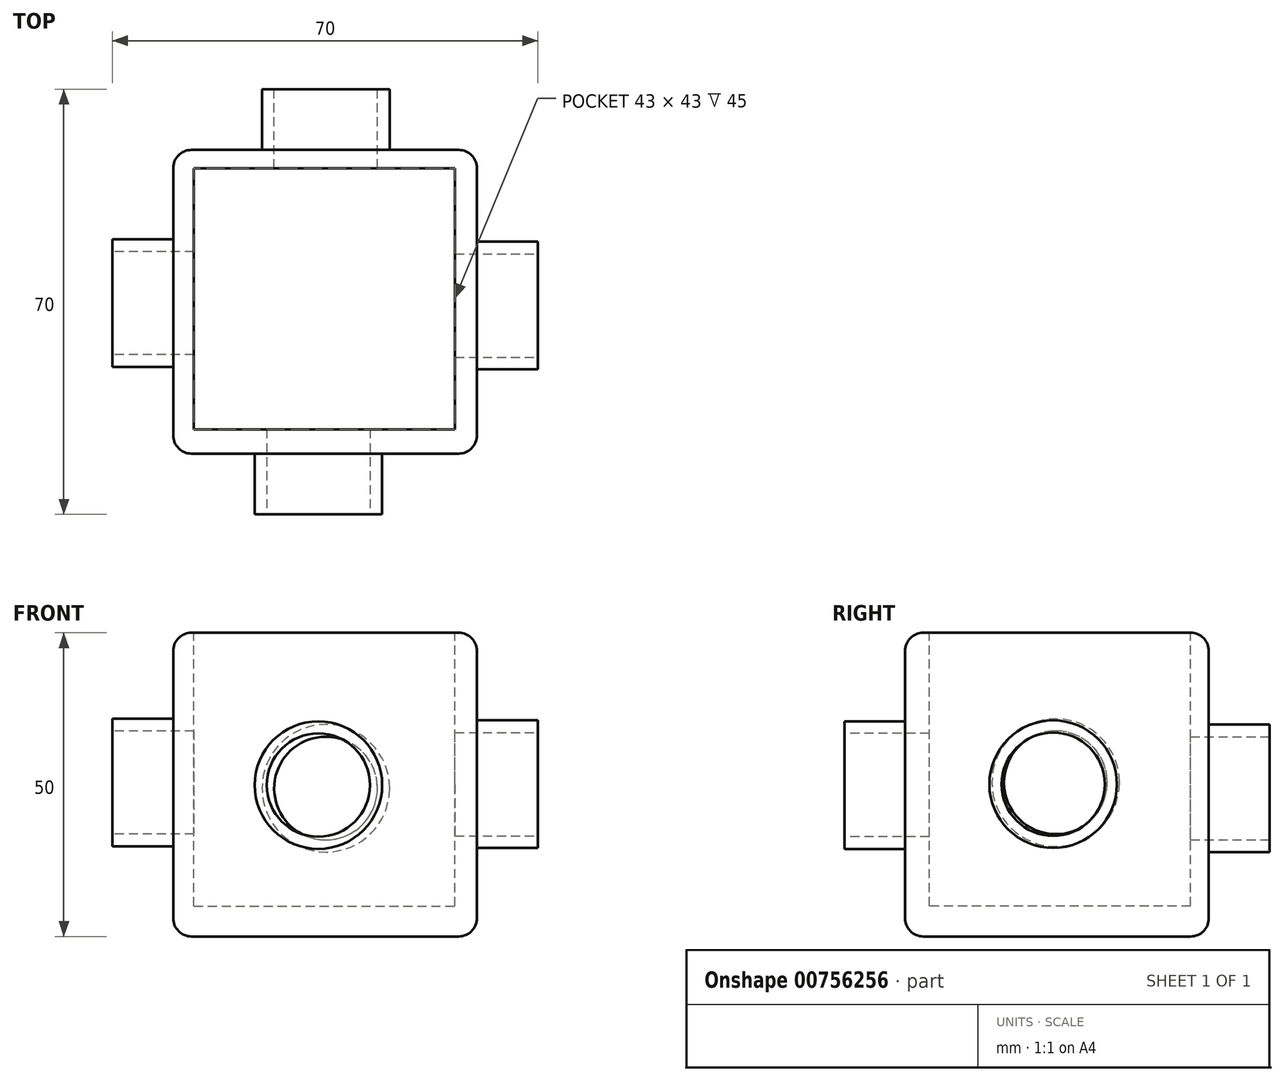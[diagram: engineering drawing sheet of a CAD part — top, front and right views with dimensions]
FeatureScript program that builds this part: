
annotation { "Feature Type Name" : "Feature", "Feature Type Description" : "" }
export const myFeature = defineFeature(function(context is Context, id is Id, definition is map)
    precondition{}
    {
        {
            var Q0;
            Q0=qCreatedBy(makeId("Top.planeOp"),FACE);
            var sketch = newSketch(context, id + "F0", { "sketchPlane" : qUnion([Q0])});
            skLineSegment(sketch, "E0.bottom", {"start": v(-55.44, -10.91) * mm, "end": v(-5.44, -10.91) * mm});
            skLineSegment(sketch, "E0.top", {"start": v(-55.44, -60.91) * mm, "end": v(-5.44, -60.91) * mm});
            skLineSegment(sketch, "E0.left", {"start": v(-55.44, -10.91) * mm, "end": v(-55.44, -60.91) * mm});
            skLineSegment(sketch, "E0.right", {"start": v(-5.44, -10.91) * mm, "end": v(-5.44, -60.91) * mm});
            skSolve(sketch);
        }
        {
            var Q0;
            Q0=qSketchRegion(id+"F0",true);
            extrude(context, id + "F1", {"entities" : qUnion([Q0]), "depth" : 50 * mm, "offsetDistance" : 25 * mm});
        }
        {
            var Q0;
            Q0=makeQuery(id+"F1.opExtrude","CAP_FACE",FACE,{"disambiguationData":[OSD([sQuery(id+"F0.wireOp",EDGE,"E0.bottom"),sQuery(id+"F0.wireOp",EDGE,"E0.top"),sQuery(id+"F0.wireOp",EDGE,"E0.left"),sQuery(id+"F0.wireOp",EDGE,"E0.right")])],"isStart":false});
            var sketch = newSketch(context, id + "F2", { "sketchPlane" : qUnion([Q0])});
            skLineSegment(sketch, "E1.bottom", {"start": v(-55.44, -60.91) * mm, "end": v(-5.44, -60.91) * mm});
            skLineSegment(sketch, "E1.top", {"start": v(-55.44, -10.91) * mm, "end": v(-5.44, -10.91) * mm});
            skLineSegment(sketch, "E1.left", {"start": v(-55.44, -60.91) * mm, "end": v(-55.44, -10.91) * mm});
            skLineSegment(sketch, "E1.right", {"start": v(-5.44, -60.91) * mm, "end": v(-5.44, -10.91) * mm});
            skSolve(sketch);
        }
        {
            var Q0;
            Q0=makeQuery(id+"F2.imprint","IMPRINT",FACE,{"disambiguationData":[TD([[makeQuery(id+"F2.imprint","IMPRINT",EDGE,{"derivedFrom":sQuery(id+"F2.wireOp",EDGE,"E1.bottom")}),1.0]])]});
            var sketch = newSketch(context, id + "F3", { "sketchPlane" : qUnion([Q0])});
            skLineSegment(sketch, "E2.bottom", {"start": v(-52.06, -13.92) * mm, "end": v(-9.06, -13.92) * mm});
            skLineSegment(sketch, "E2.top", {"start": v(-52.06, -56.92) * mm, "end": v(-9.06, -56.92) * mm});
            skLineSegment(sketch, "E2.left", {"start": v(-52.06, -13.92) * mm, "end": v(-52.06, -56.92) * mm});
            skLineSegment(sketch, "E2.right", {"start": v(-9.06, -13.92) * mm, "end": v(-9.06, -56.92) * mm});
            skSolve(sketch);
        }
        {
            var Q0;
            Q0=qSketchRegion(id+"F3",true);
            extrude(context, id + "F4", {"entities" : qUnion([Q0]), "operationType" : NewBodyOperationType.REMOVE, "oppositeDirection" : true, "depth" : 45 * mm, "offsetDistance" : 25 * mm});
        }
        {
            var Q0;
            Q0=makeQuery(id+"F1.opExtrude","SWEPT_FACE",FACE,{"disambiguationData":[OSD([sQuery(id+"F0.wireOp",EDGE,"E0.top")])]});
            var sketch = newSketch(context, id + "F5", { "sketchPlane" : qUnion([Q0])});
            skCircle(sketch, "E3", {"center": v(-31.55, 24.92) * mm, "radius": 8.5 * mm});
            skSolve(sketch);
        }
        {
            var Q0;
            Q0=makeQuery(id+"F5.imprint","IMPRINT",FACE,{"disambiguationData":[TD([[makeQuery(id+"F5.imprint","IMPRINT",EDGE,{"derivedFrom":sQuery(id+"F5.wireOp",EDGE,"E3")}),1.0]])]});
            extrude(context, id + "F6", {"entities" : qUnion([Q0]), "operationType" : NewBodyOperationType.REMOVE, "oppositeDirection" : true, "depth" : 10 * mm, "offsetDistance" : 25 * mm});
        }
        {
            var Q0;
            Q0=makeQuery(id+"F1.opExtrude","SWEPT_FACE",FACE,{"disambiguationData":[OSD([sQuery(id+"F0.wireOp",EDGE,"E0.right")])]});
            var sketch = newSketch(context, id + "F7", { "sketchPlane" : qUnion([Q0])});
            skCircle(sketch, "E4", {"center": v(-36.54, 25.07) * mm, "radius": 8.5 * mm});
            skSolve(sketch);
        }
        {
            var Q0;
            Q0=qSketchRegion(id+"F7",true);
            extrude(context, id + "F8", {"entities" : qUnion([Q0]), "operationType" : NewBodyOperationType.REMOVE, "oppositeDirection" : true, "depth" : 7 * mm, "offsetDistance" : 25 * mm});
        }
        {
            var Q0;
            Q0=makeQuery(id+"F1.opExtrude","SWEPT_FACE",FACE,{"disambiguationData":[OSD([sQuery(id+"F0.wireOp",EDGE,"E0.bottom")])]});
            var sketch = newSketch(context, id + "F9", { "sketchPlane" : qUnion([Q0])});
            skCircle(sketch, "E5", {"center": v(30.32, 24.4) * mm, "radius": 8.5 * mm});
            skSolve(sketch);
        }
        {
            var Q0;
            Q0=qSketchRegion(id+"F9",true);
            extrude(context, id + "F10", {"entities" : qUnion([Q0]), "operationType" : NewBodyOperationType.REMOVE, "oppositeDirection" : true, "depth" : 7 * mm, "offsetDistance" : 25 * mm});
        }
        {
            var Q0;
            Q0=makeQuery(id+"F1.opExtrude","SWEPT_FACE",FACE,{"disambiguationData":[OSD([sQuery(id+"F0.wireOp",EDGE,"E0.left")])]});
            var sketch = newSketch(context, id + "F11", { "sketchPlane" : qUnion([Q0])});
            skCircle(sketch, "E6", {"center": v(36.13, 25.34) * mm, "radius": 8.5 * mm});
            skSolve(sketch);
        }
        {
            var Q0;
            Q0=qSketchRegion(id+"F11",true);
            extrude(context, id + "F12", {"entities" : qUnion([Q0]), "operationType" : NewBodyOperationType.REMOVE, "oppositeDirection" : true, "depth" : 7 * mm, "offsetDistance" : 25 * mm});
        }
        {
            var Q0;
            Q0=makeQuery(id+"F1.opExtrude","SWEPT_FACE",FACE,{"disambiguationData":[OSD([sQuery(id+"F0.wireOp",EDGE,"E0.left")])]});
            var sketch = newSketch(context, id + "F13", { "sketchPlane" : qUnion([Q0])});
            skCircle(sketch, "E7", {"center": v(36.13, 25.34) * mm, "radius": 10.5 * mm});
            skSolve(sketch);
        }
        {
            var Q0;
            Q0=makeQuery(id+"F13.imprint","IMPRINT",FACE,{"disambiguationData":[TD([[makeQuery(id+"F13.imprint","IMPRINT",EDGE,{"derivedFrom":sQuery(id+"F13.wireOp",EDGE,"E7")}),1.0]])]});
            extrude(context, id + "F14", {"entities" : qUnion([Q0]), "operationType" : NewBodyOperationType.ADD, "depth" : 10 * mm, "offsetDistance" : 25 * mm});
        }
        {
            var Q0;
            Q0=makeQuery(id+"F1.opExtrude","SWEPT_FACE",FACE,{"disambiguationData":[OSD([sQuery(id+"F0.wireOp",EDGE,"E0.top")])]});
            var sketch = newSketch(context, id + "F15", { "sketchPlane" : qUnion([Q0])});
            skCircle(sketch, "E8", {"center": v(-31.55, 24.92) * mm, "radius": 10.5 * mm});
            skSolve(sketch);
        }
        {
            var Q0;
            Q0=makeQuery(id+"F15.imprint","IMPRINT",FACE,{"disambiguationData":[TD([[makeQuery(id+"F15.imprint","IMPRINT",EDGE,{"derivedFrom":sQuery(id+"F15.wireOp",EDGE,"E8")}),1.0]])]});
            extrude(context, id + "F16", {"entities" : qUnion([Q0]), "operationType" : NewBodyOperationType.ADD, "depth" : 10 * mm, "offsetDistance" : 25 * mm});
        }
        {
            var Q0;
            Q0=makeQuery(id+"F1.opExtrude","SWEPT_FACE",FACE,{"disambiguationData":[OSD([sQuery(id+"F0.wireOp",EDGE,"E0.right")])]});
            var sketch = newSketch(context, id + "F17", { "sketchPlane" : qUnion([Q0])});
            skCircle(sketch, "E9", {"center": v(-36.54, 25.07) * mm, "radius": 10.5 * mm});
            skSolve(sketch);
        }
        {
            var Q0;
            Q0=makeQuery(id+"F17.imprint","IMPRINT",FACE,{"disambiguationData":[TD([[makeQuery(id+"F17.imprint","IMPRINT",EDGE,{"derivedFrom":sQuery(id+"F17.wireOp",EDGE,"E9")}),1.0]])]});
            extrude(context, id + "F18", {"entities" : qUnion([Q0]), "operationType" : NewBodyOperationType.ADD, "depth" : 10 * mm, "offsetDistance" : 25 * mm});
        }
        {
            var Q0;
            Q0=makeQuery(id+"F1.opExtrude","SWEPT_FACE",FACE,{"disambiguationData":[OSD([sQuery(id+"F0.wireOp",EDGE,"E0.bottom")])]});
            var sketch = newSketch(context, id + "F19", { "sketchPlane" : qUnion([Q0])});
            skCircle(sketch, "E10", {"center": v(30.32, 24.4) * mm, "radius": 10.5 * mm});
            skSolve(sketch);
        }
        {
            var Q0;
            Q0=makeQuery(id+"F19.imprint","IMPRINT",FACE,{"disambiguationData":[TD([[makeQuery(id+"F19.imprint","IMPRINT",EDGE,{"derivedFrom":sQuery(id+"F19.wireOp",EDGE,"E10")}),1.0]])]});
            extrude(context, id + "F20", {"entities" : qUnion([Q0]), "operationType" : NewBodyOperationType.ADD, "depth" : 10 * mm, "offsetDistance" : 25 * mm});
        }
        {
            var Q0;
            Q0=makeQuery(id+"F1.opExtrude","CAP_EDGE",EDGE,{"disambiguationData":[OSD([sQuery(id+"F0.wireOp",EDGE,"E0.right")])],"isStart":false});
            fillet(context, id + "F21", {"entities" : qUnion([Q0]), "radius" : 3 * mm, "tangentPropagation" : true, "allowEdgeOverflow" : false});
        }
        {
            var Q0;
            Q0=makeQuery(id+"F1.opExtrude","CAP_EDGE",EDGE,{"disambiguationData":[OSD([sQuery(id+"F0.wireOp",EDGE,"E0.bottom")])],"isStart":false});
            fillet(context, id + "F22", {"entities" : qUnion([Q0]), "radius" : 3 * mm, "tangentPropagation" : true, "allowEdgeOverflow" : false});
        }
        {
            var Q0;
            Q0=makeQuery(id+"F1.opExtrude","CAP_EDGE",EDGE,{"disambiguationData":[OSD([sQuery(id+"F0.wireOp",EDGE,"E0.top")])],"isStart":false});
            fillet(context, id + "F23", {"entities" : qUnion([Q0]), "radius" : 3 * mm, "tangentPropagation" : true, "allowEdgeOverflow" : false});
        }
        {
            var Q0;
            Q0=makeQuery(id+"F1.opExtrude","CAP_EDGE",EDGE,{"disambiguationData":[OSD([sQuery(id+"F0.wireOp",EDGE,"E0.left")])],"isStart":false});
            fillet(context, id + "F24", {"entities" : qUnion([Q0]), "radius" : 3 * mm, "tangentPropagation" : true, "allowEdgeOverflow" : false});
        }
        {
            var Q0;
            Q0=makeQuery(id+"F1.opExtrude","CAP_EDGE",EDGE,{"disambiguationData":[OSD([sQuery(id+"F0.wireOp",EDGE,"E0.top")])],"isStart":true});
            fillet(context, id + "F25", {"entities" : qUnion([Q0]), "radius" : 3 * mm, "tangentPropagation" : true, "allowEdgeOverflow" : false});
        }
    });
